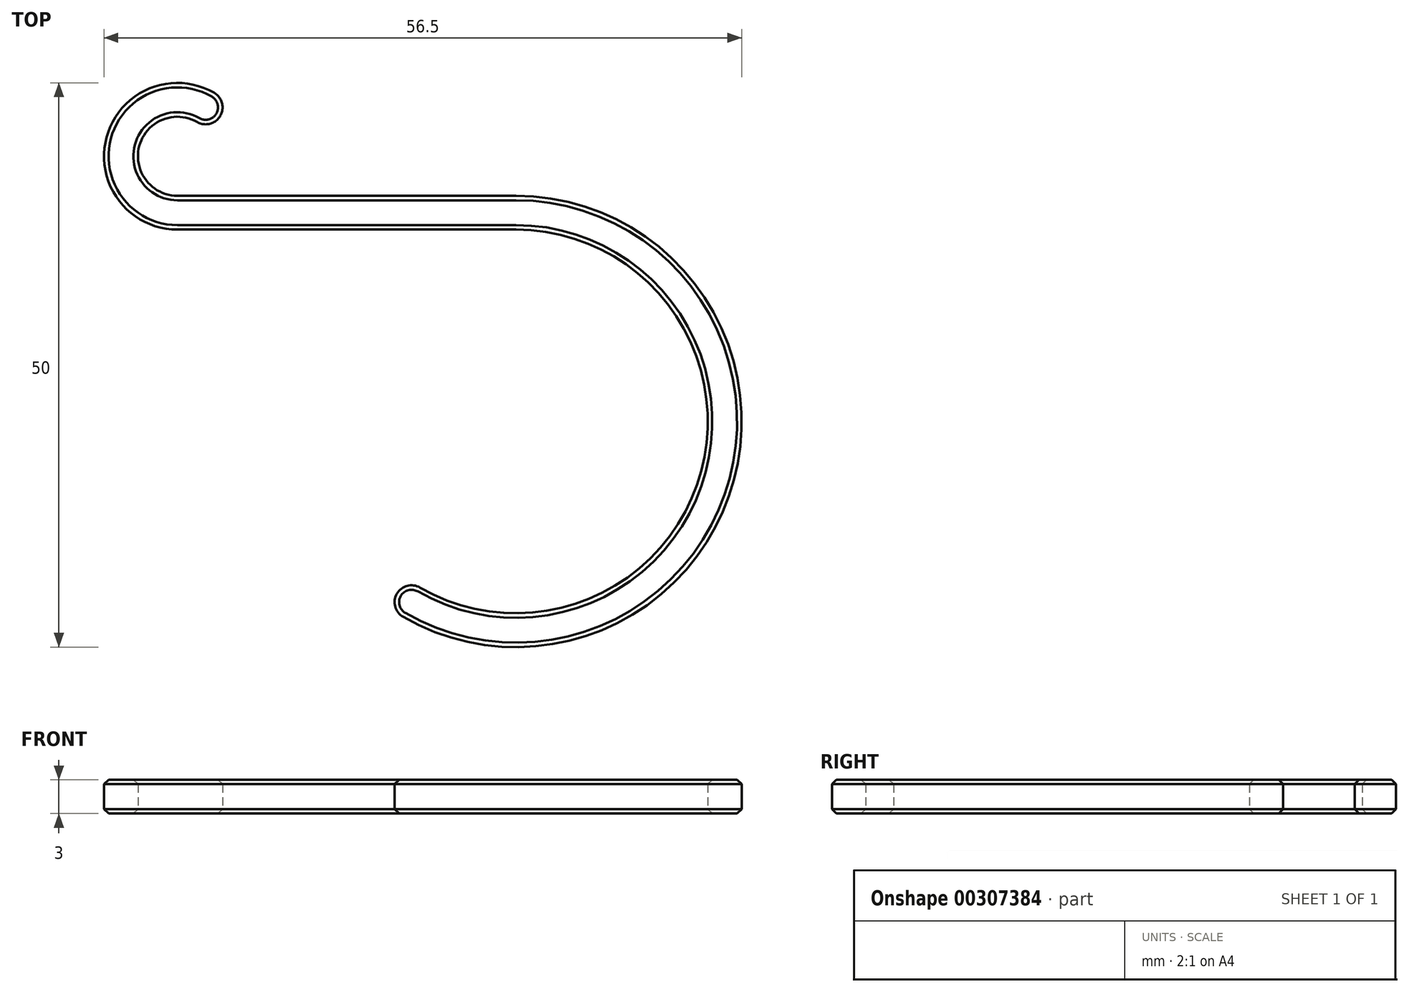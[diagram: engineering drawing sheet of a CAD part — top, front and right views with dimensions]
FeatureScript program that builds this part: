
annotation { "Feature Type Name" : "Feature", "Feature Type Description" : "" }
export const myFeature = defineFeature(function(context is Context, id is Id, definition is map)
    precondition{}
    {
        {
            assignVariable(context, id + "F0", {"name" : "hookWidth", "anyValue" : 3 * mm});
        }
        {
            var Q0;
            Q0=qCreatedBy(makeId("Top.planeOp"),FACE);
            var sketch = newSketch(context, id + "F1", { "sketchPlane" : qUnion([Q0])});
            skArc(sketch, "E0", {"start": v(-8.5, -14.72) * mm, "mid": v(16.42, -4.4) * mm, "end": v(0, 17) * mm});
            skLineSegment(sketch, "E1", {"start": v(0, 20) * mm, "end": v(-30, 20) * mm});
            skArc(sketch, "E2", {"start": v(-30, 20) * mm, "mid": v(-33.38, 24.4) * mm, "end": v(-28.25, 26.53) * mm});
            skLineSegment(sketch, "E3", {"start": v(0, 0) * mm, "end": v(0, 17) * mm, "construction": true});
            skLineSegment(sketch, "E4", {"start": v(0, 0) * mm, "end": v(-8.5, -14.72) * mm, "construction": true});
            skLineSegment(sketch, "E5", {"start": v(-30, 20) * mm, "end": v(-30, 23.5) * mm, "construction": true});
            skLineSegment(sketch, "E6", {"start": v(-30, 23.5) * mm, "end": v(-28.25, 26.53) * mm, "construction": true});
            skArc(sketch, "E7", {"start": v(-10, -17.32) * mm, "mid": v(19.32, -5.18) * mm, "end": v(0, 20) * mm});
            skLineSegment(sketch, "E8", {"start": v(0, 17) * mm, "end": v(-30, 17) * mm});
            skArc(sketch, "E9", {"start": v(-30, 17) * mm, "mid": v(-36.28, 25.18) * mm, "end": v(-26.75, 29.13) * mm});
            skLineSegment(sketch, "E10", {"start": v(-8.5, -14.72) * mm, "end": v(-10, -17.32) * mm, "construction": true});
            skLineSegment(sketch, "E11", {"start": v(-28.25, 26.53) * mm, "end": v(-26.75, 29.13) * mm, "construction": true});
            skArc(sketch, "E12", {"start": v(-26.75, 29.13) * mm, "mid": v(-26.2, 27.08) * mm, "end": v(-28.25, 26.53) * mm});
            skArc(sketch, "E13", {"start": v(-8.5, -14.72) * mm, "mid": v(-10.55, -15.27) * mm, "end": v(-10, -17.32) * mm});
            skSolve(sketch);
        }
        {
            var Q0;
            Q0=makeQuery(id+"F1.imprint","IMPRINT",FACE,{"disambiguationData":[TD([[makeQuery(id+"F1.imprint","IMPRINT",EDGE,{"derivedFrom":sQuery(id+"F1.wireOp",EDGE,"E0")}),-1.0]])]});
            extrude(context, id + "F2", {"entities" : qUnion([Q0]), "depth" : getVariable(context, 'hookWidth')});
        }
        {
            var Q0;
            Q0=makeQuery(id+"F2.opExtrude","CAP_EDGE",EDGE,{"disambiguationData":[OSD([sQuery(id+"F1.wireOp",EDGE,"E8")])],"isStart":false});
            var Q1;
            Q1=makeQuery(id+"F2.opExtrude","CAP_EDGE",EDGE,{"disambiguationData":[OSD([sQuery(id+"F1.wireOp",EDGE,"E8")])],"isStart":true});
            chamfer(context, id + "F3", {"entities" : qUnion([Q0, Q1]), "width" : 0.4 * mm, "tangentPropagation" : true});
        }
    });
